# Revit family: TYCO-FPP-FireClass - FC410QIO QUAD IO MODULE
name_source: partatom
category: Electrical Fixtures
revit_build: Autodesk Revit 2014 (Build: 20130308_1515(x64)
units: mm (PartAtom-declared; Revit-internal decimal feet)

## types (1)
- TYCO-FPP-FireClass - FC410QIO QUAD IO MODULE
    Approvals = EN54-17, EN54-18 and
EN54-13
    Description = Quad Input/ Output Unit
    Input EOL = 3k3 Ohm
    Keynote = The FC410QIO Quad Input/Output Module is designed to
provide four monitored digital inputs and four potential free relay
changeover outputs.
    Length = 96 mm
    Manufacturer = Tyco
    Model = FireClass - 555.800.771
    Operating Humidity = Up to 95 %
    Operating Temperature = -20 to +70 oC
    PCB = PCB
    RS = RS
    RSS = res
    Relay Output = 2A@30Vdc
    ST = ST12
    Storage Temparature = 40 to +80 oC
    Type Comments = The digital input monitoring and isolator functions are both
configurable.
    URL = https://fireclass.co.uk
    Width = 134 mm

## geometry (parser evidence)
native form markers: Sweep x1
no freeform markers — native parametric forms only
